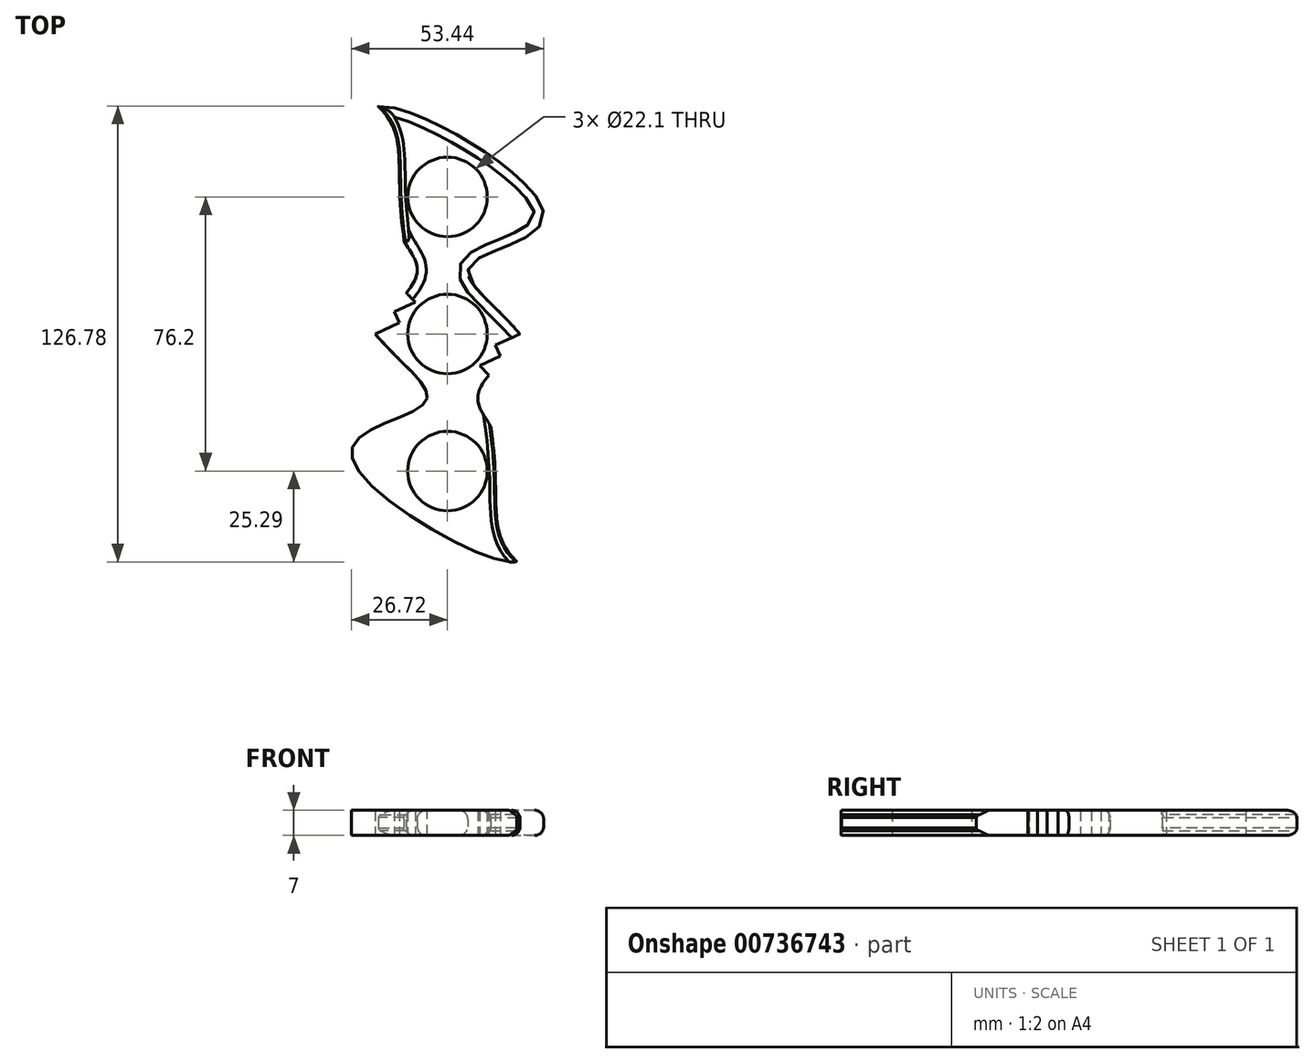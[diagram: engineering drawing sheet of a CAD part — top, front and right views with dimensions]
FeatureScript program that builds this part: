
annotation { "Feature Type Name" : "Feature", "Feature Type Description" : "" }
export const myFeature = defineFeature(function(context is Context, id is Id, definition is map)
    precondition{}
    {
        {
            var Q0;
            Q0=qCreatedBy(makeId("Top.planeOp"),FACE);
            var sketch = newSketch(context, id + "F0", { "sketchPlane" : qUnion([Q0])});
            skCircle(sketch, "E0", {"center": v(0, 0) * mm, "radius": 11.05 * mm});
            skPoint(sketch, "E1", {"position": v(0, 38.1) * mm});
            skCircle(sketch, "E2", {"center": v(0, 38.1) * mm, "radius": 11.05 * mm});
            skLineSegment(sketch, "E3", {"start": v(0, 0) * mm, "end": v(0, 0) * mm});
            skLineSegment(sketch, "E4.MirrorCS", {"start": v(13.35, -3.13) * mm, "end": v(20.17, 0) * mm});
            skLineSegment(sketch, "E5.MirrorCS", {"start": v(14.73, -6.15) * mm, "end": v(13.35, -3.13) * mm});
            skLineSegment(sketch, "E6.MirrorCS", {"start": v(8.93, -8.82) * mm, "end": v(14.73, -6.15) * mm});
            skLineSegment(sketch, "E7.MirrorCS", {"start": v(11.47, -11.45) * mm, "end": v(8.93, -8.82) * mm});
            skFitSpline(sketch, "E8.MirrorCS", {"points": [v(-20.17, 0) * mm, v(-6.36, -19.22) * mm, v(-26.72, -33.11) * mm, v(19.26, -63.26) * mm, v(16.09, -45.99) * mm, v(12.06, -25.84) * mm, v(11.47, -11.45) * mm], "startDerivative": vector(143.44, -167.96) * mm, "endDerivative": vector(144.1, 165.7) * mm});
            skFitSpline(sketch, "E9.MirrorCS", {"points": [v(19.26, -63.26) * mm, v(14.35, -55.19) * mm, v(13.33, -41.15) * mm, v(12.06, -25.84) * mm], "startDerivative": vector(-25.48, 24.54) * mm, "endDerivative": vector(-5.96, 41.82) * mm});
            skFitSpline(sketch, "E10.MirrorCS", {"points": [v(-20.17, 0) * mm, v(-6.36, -19.22) * mm, v(-26.72, -33.11) * mm, v(19.26, -63.26) * mm, v(16.09, -45.99) * mm, v(12.06, -25.84) * mm, v(11.47, -11.45) * mm], "startDerivative": vector(143.44, -167.96) * mm, "endDerivative": vector(144.1, 165.7) * mm});
            skCircle(sketch, "E11.MirrorC", {"center": v(0, -38.1) * mm, "radius": 11.05 * mm});
            skFitSpline(sketch, "E12.MirrorCS", {"points": [v(20.17, 0) * mm, v(6.36, 19.22) * mm, v(26.72, 33.11) * mm, v(-19.26, 63.26) * mm, v(-16.09, 45.99) * mm, v(-12.06, 25.84) * mm, v(-11.47, 11.45) * mm], "startDerivative": vector(-143.44, 167.96) * mm, "endDerivative": vector(-144.1, -165.7) * mm});
            skFitSpline(sketch, "E13.MirrorCS", {"points": [v(-19.26, 63.26) * mm, v(-14.35, 55.19) * mm, v(-13.33, 41.15) * mm, v(-12.06, 25.84) * mm], "startDerivative": vector(25.48, -24.54) * mm, "endDerivative": vector(5.96, -41.82) * mm});
            skFitSpline(sketch, "E14.MirrorCS", {"points": [v(20.17, 0) * mm, v(6.36, 19.22) * mm, v(26.72, 33.11) * mm, v(-19.26, 63.26) * mm, v(-16.09, 45.99) * mm, v(-12.06, 25.84) * mm, v(-11.47, 11.45) * mm], "startDerivative": vector(-143.44, 167.96) * mm, "endDerivative": vector(-144.1, -165.7) * mm});
            skLineSegment(sketch, "E15.MirrorCS", {"start": v(-11.47, 11.45) * mm, "end": v(-8.93, 8.82) * mm});
            skLineSegment(sketch, "E16.MirrorCS", {"start": v(-8.93, 8.82) * mm, "end": v(-14.73, 6.15) * mm});
            skLineSegment(sketch, "E17.MirrorCS", {"start": v(-14.73, 6.15) * mm, "end": v(-13.35, 3.13) * mm});
            skLineSegment(sketch, "E18.MirrorCS", {"start": v(-13.35, 3.13) * mm, "end": v(-20.17, 0) * mm});
            skPoint(sketch, "E19.3.internal.orphan", {"position": v(19.26, 63.26) * mm});
            skPoint(sketch, "E19.5.internal.orphan", {"position": v(12.06, 25.84) * mm});
            skPoint(sketch, "E20.orphan", {"position": v(8.93, 8.82) * mm});
            skPoint(sketch, "E21.start.orphan", {"position": v(11.47, 11.45) * mm});
            skPoint(sketch, "E22.start.orphan", {"position": v(13.35, 3.13) * mm});
            skPoint(sketch, "E23.end.orphan", {"position": v(14.73, 6.15) * mm});
            skSolve(sketch);
        }
        {
            var Q0;
            Q0=makeQuery(id+"F0.imprint","IMPRINT",FACE,{"disambiguationData":[TD([[makeQuery(id+"F0.imprint","IMPRINT",EDGE,{"derivedFrom":sQuery(id+"F0.wireOp",EDGE,"E0")}),-1.0]])]});
            extrude(context, id + "F1", {"entities" : qUnion([Q0]), "depth" : 7 * mm, "offsetDistance" : 25.4 * mm});
        }
        {
            var Q0;
            Q0=makeQuery(id+"F1.opExtrude","CAP_EDGE",EDGE,{"disambiguationData":[OSD([sQuery(id+"F0.wireOp",EDGE,"E11.MirrorC")])],"isStart":false});
            var Q1;
            Q1=makeQuery(id+"F1.opExtrude","CAP_EDGE",EDGE,{"disambiguationData":[OSD([sQuery(id+"F0.wireOp",EDGE,"E0")])],"isStart":false});
            var Q2;
            Q2=makeQuery(id+"F1.opExtrude","CAP_EDGE",EDGE,{"disambiguationData":[OSD([sQuery(id+"F0.wireOp",EDGE,"E2")])],"isStart":false});
            fillet(context, id + "F2", {"entities" : qUnion([Q0, Q1, Q2]), "radius" : .1 * mm, "tangentPropagation" : true, "allowEdgeOverflow" : false});
        }
        {
            var Q0;
            Q0=makeQuery(id+"F1.opExtrude","CAP_EDGE",EDGE,{"disambiguationData":[OSD([sQuery(id+"F0.wireOp",EDGE,"E9.MirrorCS")])],"isStart":false});
            var Q1;
            Q1=makeQuery(id+"F1.opExtrude","CAP_EDGE",EDGE,{"disambiguationData":[OSD([sQuery(id+"F0.wireOp",EDGE,"E9.MirrorCS")])],"isStart":true});
            var Q2;
            Q2=makeQuery(id+"F1.opExtrude","CAP_EDGE",EDGE,{"disambiguationData":[OSD([sQuery(id+"F0.wireOp",EDGE,"E13.MirrorCS")])],"isStart":false});
            var Q3;
            Q3=makeQuery(id+"F1.opExtrude","CAP_EDGE",EDGE,{"disambiguationData":[OSD([sQuery(id+"F0.wireOp",EDGE,"E13.MirrorCS")])],"isStart":true});
            chamfer(context, id + "F3", {"entities" : qUnion([Q0, Q1, Q2, Q3]), "width" : 1.6 * mm, "tangentPropagation" : true});
        }
        {
            var Q0;
            {var subQ0=sQuery(id+"F0.wireOp",EDGE,"E9.MirrorCS");Q0=makeQuery(id+"F3.opChamfer","BLEND_EDGE",EDGE,{"blendedFrom":[makeQuery(id+"F1.opExtrude","CAP_EDGE",EDGE,{"disambiguationData":[OSD([subQ0])],"isStart":false}),makeQuery(id+"F1.opExtrude","SWEPT_FACE",FACE,{"disambiguationData":[OSD([subQ0])]})],"blendedInto":[makeQuery(id+"F1.opExtrude","SWEPT_FACE",FACE,{"disambiguationData":[OSD([subQ0])]})]});}
            var Q1;
            {var subQ0=sQuery(id+"F0.wireOp",EDGE,"E9.MirrorCS");Q1=makeQuery(id+"F3.opChamfer","BLEND_EDGE",EDGE,{"blendedFrom":[makeQuery(id+"F1.opExtrude","CAP_EDGE",EDGE,{"disambiguationData":[OSD([subQ0])],"isStart":true}),makeQuery(id+"F1.opExtrude","SWEPT_FACE",FACE,{"disambiguationData":[OSD([subQ0])]})],"blendedInto":[makeQuery(id+"F1.opExtrude","SWEPT_FACE",FACE,{"disambiguationData":[OSD([subQ0])]})]});}
            var Q2;
            {var subQ0=sQuery(id+"F0.wireOp",EDGE,"E13.MirrorCS");Q2=makeQuery(id+"F3.opChamfer","BLEND_EDGE",EDGE,{"blendedFrom":[makeQuery(id+"F1.opExtrude","CAP_EDGE",EDGE,{"disambiguationData":[OSD([subQ0])],"isStart":false}),makeQuery(id+"F1.opExtrude","SWEPT_FACE",FACE,{"disambiguationData":[OSD([subQ0])]})],"blendedInto":[makeQuery(id+"F1.opExtrude","SWEPT_FACE",FACE,{"disambiguationData":[OSD([subQ0])]})]});}
            var Q3;
            {var subQ0=sQuery(id+"F0.wireOp",EDGE,"E13.MirrorCS");Q3=makeQuery(id+"F3.opChamfer","BLEND_EDGE",EDGE,{"blendedFrom":[makeQuery(id+"F1.opExtrude","CAP_EDGE",EDGE,{"disambiguationData":[OSD([subQ0])],"isStart":true}),makeQuery(id+"F1.opExtrude","SWEPT_FACE",FACE,{"disambiguationData":[OSD([subQ0])]})],"blendedInto":[makeQuery(id+"F1.opExtrude","SWEPT_FACE",FACE,{"disambiguationData":[OSD([subQ0])]})]});}
            fillet(context, id + "F4", {"entities" : qUnion([Q0, Q1, Q2, Q3]), "radius" : 1 * mm, "tangentPropagation" : true, "allowEdgeOverflow" : false});
        }
        {
            var Q0;
            Q0=makeQuery(id+"F1.opExtrude","CAP_EDGE",EDGE,{"disambiguationData":[OSD([sQuery(id+"F0.wireOp",EDGE,"E12.MirrorCS")])],"isStart":false});
            var Q1;
            Q1=makeQuery(id+"F1.opExtrude","CAP_EDGE",EDGE,{"disambiguationData":[OSD([sQuery(id+"F0.wireOp",EDGE,"E12.MirrorCS")])],"isStart":true});
            var Q2;
            Q2=makeQuery(id+"F1.opExtrude","CAP_EDGE",EDGE,{"disambiguationData":[OSD([sQuery(id+"F0.wireOp",EDGE,"E10.MirrorCS")])],"isStart":false});
            var Q3;
            Q3=makeQuery(id+"F1.opExtrude","CAP_EDGE",EDGE,{"disambiguationData":[OSD([sQuery(id+"F0.wireOp",EDGE,"E10.MirrorCS")])],"isStart":true});
            fillet(context, id + "F5", {"entities" : qUnion([Q0, Q1, Q2, Q3]), "radius" : 2.5 * mm, "tangentPropagation" : true, "allowEdgeOverflow" : false});
        }
    });
